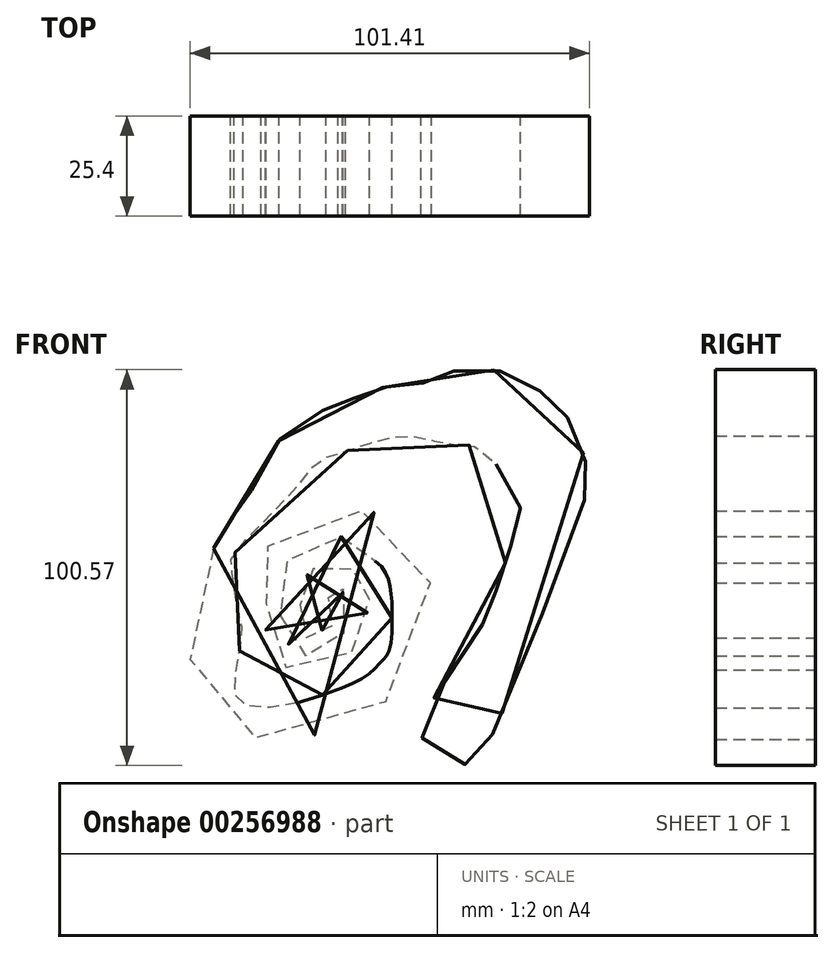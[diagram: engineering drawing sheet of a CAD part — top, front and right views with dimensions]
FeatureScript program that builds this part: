
annotation { "Feature Type Name" : "Feature", "Feature Type Description" : "" }
export const myFeature = defineFeature(function(context is Context, id is Id, definition is map)
    precondition{}
    {
        {
            var Q0;
            Q0=qCreatedBy(makeId("Front.planeOp"),FACE);
            var sketch = newSketch(context, id + "F0", { "sketchPlane" : qUnion([Q0])});
            skFitSpline(sketch, "E0", {"points": [v(-64.97, 31.8) * mm, v(-66.5, -10.3) * mm, v(-16.55, -2.33) * mm, v(-19.92, 39.6) * mm, v(-51.79, 31.63) * mm, v(-51.79, 21.82) * mm, v(-49.34, 3.22) * mm, v(-32.48, 3.5) * mm, v(-26.97, 11.52) * mm, v(-25.74, 21.99) * mm, v(-28.5, 25.18) * mm, v(-30.34, 27.1) * mm, v(-37.08, 27.9) * mm, v(-41.68, 24.44) * mm, v(-42.9, 19.18) * mm, v(-42.9, 12.74) * mm, v(-41.98, 9.33) * mm, v(-40.45, 9.47) * mm, v(-38.3, 10.7) * mm, v(-34.63, 12.37) * mm, v(-33.4, 15.18) * mm, v(-34.94, 18.1) * mm, v(-36.16, 22.04) * mm, v(-32.48, 22.8) * mm, v(-32.18, 19.82) * mm, v(-31.56, 12.03) * mm, v(-34.94, 6.77) * mm, v(-42.3, 4.65) * mm, v(-46.58, 8.92) * mm, v(-48.11, 25.34) * mm, v(-44.44, 30.08) * mm, v(-32.18, 34.84) * mm, v(-28.5, 32.22) * mm, v(-22.37, 27.25) * mm, v(-20.23, 22.35) * mm, v(-19.61, 15.18) * mm, v(-20.53, 5.41) * mm, v(-22.06, 3.44) * mm, v(-25.44, 0) * mm, v(-35.85, -4.83) * mm, v(-49.64, -8.5) * mm, v(-58.53, -7.1) * mm, v(-59.45, 0) * mm, v(-57.61, 11.87) * mm, v(-57.92, 12.09) * mm, v(-59.45, 19.92) * mm, v(-60.37, 26.09) * mm, v(-60.37, 29.46) * mm, v(-45.35, 45.75) * mm, v(-38.3, 53.9) * mm, v(-32.18, 56.3) * mm, v(-21.15, 59.78) * mm, v(-12.56, 60.11) * mm, v(-4.9, 58.34) * mm, v(3.68, 56.53) * mm, v(12.87, 42.63) * mm, v(12.87, 41.72) * mm, v(10.11, 31.11) * mm, v(6.74, 20.95) * mm, v(5.52, 16.6) * mm, v(-4.9, 0) * mm, v(-11.65, -17.15) * mm, v(0, -23.2) * mm, v(3.37, -20.78) * mm, v(29.73, 45.66) * mm, v(30.03, 51.88) * mm, v(26.05, 63.6) * mm, v(21.45, 68.1) * mm, v(14.4, 74.95) * mm, v(3.37, 77.28) * mm, v(-6.13, 76.38) * mm, v(-11.03, 74.04) * mm, v(-16.55, 73.37) * mm, v(-25.13, 72.12) * mm, v(-29.42, 69.96) * mm, v(-34.02, 67.4) * mm, v(-44.13, 64.49) * mm, v(-54.55, 47.69) * mm, v(-57.92, 43.65) * mm, v(-60.98, 38.48) * mm, v(-64.97, 31.8) * mm]});
            skSolve(sketch);
        }
        {
            var Q0;
            Q0=makeQuery(id+"F0.imprint","IMPRINT",FACE,{"disambiguationData":[TD([[makeQuery(id+"F0.imprint","IMPRINT",EDGE,{"derivedFrom":sQuery(id+"F0.wireOp",EDGE,"E0")}),1.0]])]});
            extrude(context, id + "F1", {"entities" : qUnion([Q0]), "depth" : 25.4 * mm});
        }
    });
